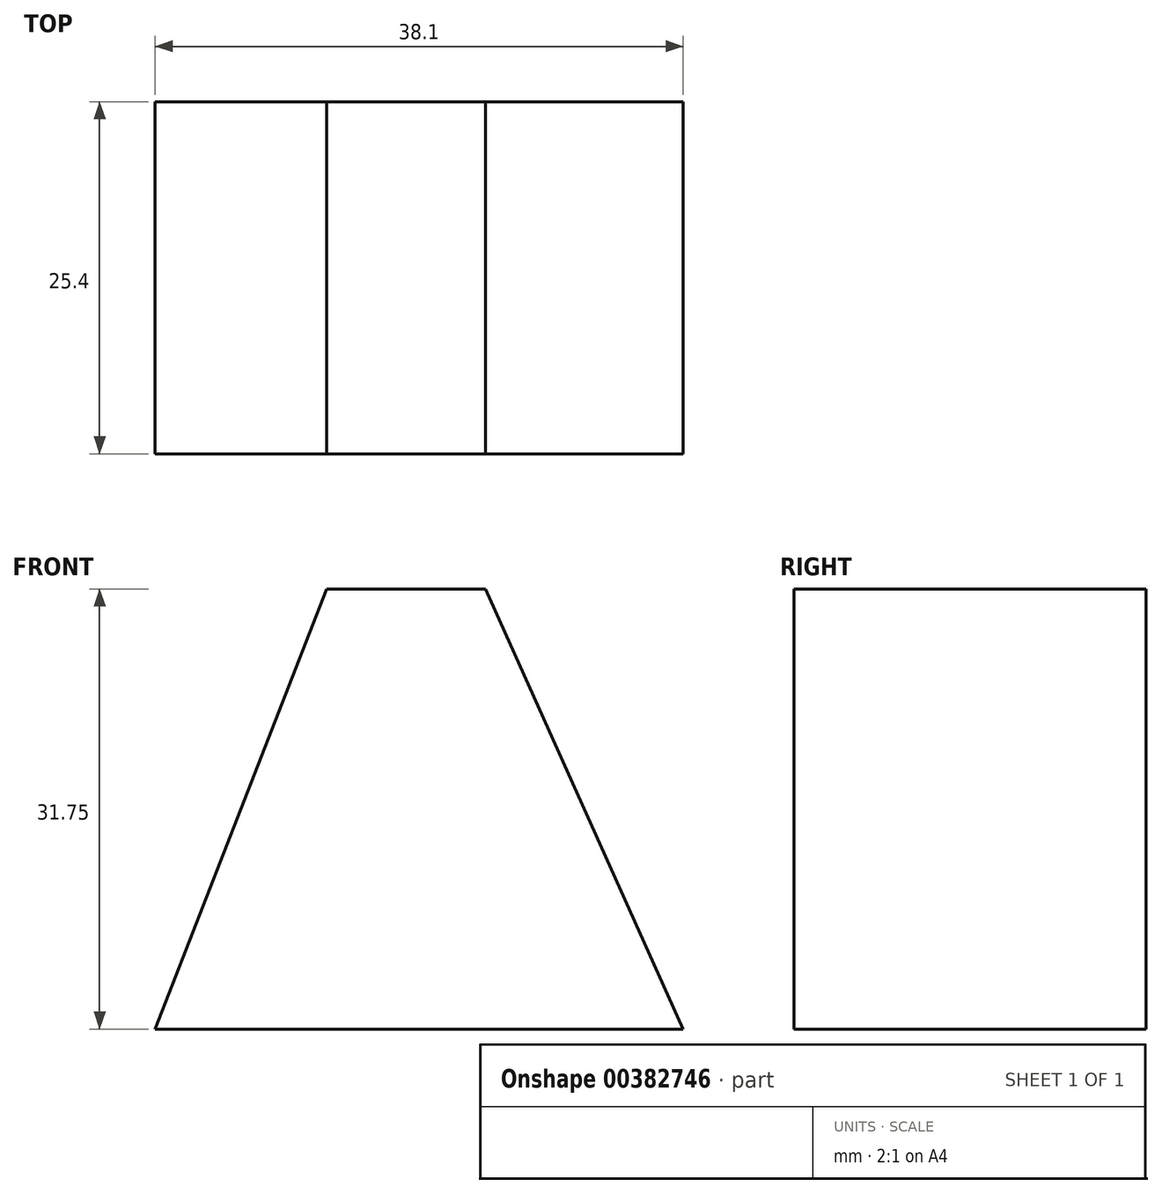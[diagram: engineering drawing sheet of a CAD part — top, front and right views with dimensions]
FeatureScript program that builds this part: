
annotation { "Feature Type Name" : "Feature", "Feature Type Description" : "" }
export const myFeature = defineFeature(function(context is Context, id is Id, definition is map)
    precondition{}
    {
        {
            var Q0;
            Q0=qCreatedBy(makeId("Front.planeOp"),FACE);
            var sketch = newSketch(context, id + "F0", { "sketchPlane" : qUnion([Q0])});
            skLineSegment(sketch, "E0", {"start": v(0, 0) * mm, "end": v(38.1, 0) * mm});
            skLineSegment(sketch, "E1", {"start": v(38.1, 31.75) * mm, "end": v(0, 31.75) * mm});
            skLineSegment(sketch, "E2", {"start": v(0, 31.75) * mm, "end": v(0, 0) * mm});
            skLineSegment(sketch, "E3", {"start": v(38.1, 31.75) * mm, "end": v(38.1, 0) * mm});
            skSolve(sketch);
        }
        {
            var Q0;
            Q0=makeQuery(id+"F0.imprint","IMPRINT",FACE,{"disambiguationData":[TD([[makeQuery(id+"F0.imprint","IMPRINT",EDGE,{"derivedFrom":sQuery(id+"F0.wireOp",EDGE,"E0")}),1.0]])]});
            extrude(context, id + "F1", {"entities" : qUnion([Q0]), "depth" : 25.4 * mm});
        }
        {
            var Q0;
            Q0=makeQuery(id+"F1.opExtrude","CAP_FACE",FACE,{"disambiguationData":[OSD([sQuery(id+"F0.wireOp",EDGE,"E0"),sQuery(id+"F0.wireOp",EDGE,"E1"),sQuery(id+"F0.wireOp",EDGE,"E2"),sQuery(id+"F0.wireOp",EDGE,"E3")])],"isStart":false});
            var sketch = newSketch(context, id + "F2", { "sketchPlane" : qUnion([Q0])});
            skLineSegment(sketch, "E4", {"start": v(0, 0) * mm, "end": v(12.38, 31.75) * mm});
            skLineSegment(sketch, "E5", {"start": v(38.1, 0) * mm, "end": v(23.83, 31.75) * mm});
            skLineSegment(sketch, "E6", {"start": v(0, 0) * mm, "end": v(13.62, 0) * mm});
            skLineSegment(sketch, "E7", {"start": v(13.62, 0) * mm, "end": v(13.62, 6.35) * mm});
            skLineSegment(sketch, "E8", {"start": v(11.44, 6.35) * mm, "end": v(24.14, 6.35) * mm});
            skLineSegment(sketch, "E9", {"start": v(24.14, 6.35) * mm, "end": v(24.14, 0) * mm});
            skLineSegment(sketch, "E10", {"start": v(24.14, 0) * mm, "end": v(38.1, 0) * mm});
            skSolve(sketch);
        }
        {
            var Q0;
            {var subQ0=sQuery(id+"F2.wireOp",EDGE,"E4");Q0=makeQuery(id+"F2.imprint","IMPRINT",FACE,{"disambiguationData":[TD([[makeQuery(id+"F2.imprint","IMPRINT",EDGE,{"derivedFrom":subQ0}),1.0]])]});}
            var Q1;
            {var subQ0=sQuery(id+"F2.wireOp",EDGE,"E5");Q1=makeQuery(id+"F2.imprint","IMPRINT",FACE,{"disambiguationData":[TD([[makeQuery(id+"F2.imprint","IMPRINT",EDGE,{"derivedFrom":subQ0}),-1.0]])]});}
            extrude(context, id + "F3", {"entities" : qUnion([Q0, Q1]), "operationType" : NewBodyOperationType.REMOVE, "oppositeDirection" : true, "depth" : 25.4 * mm});
        }
    });
